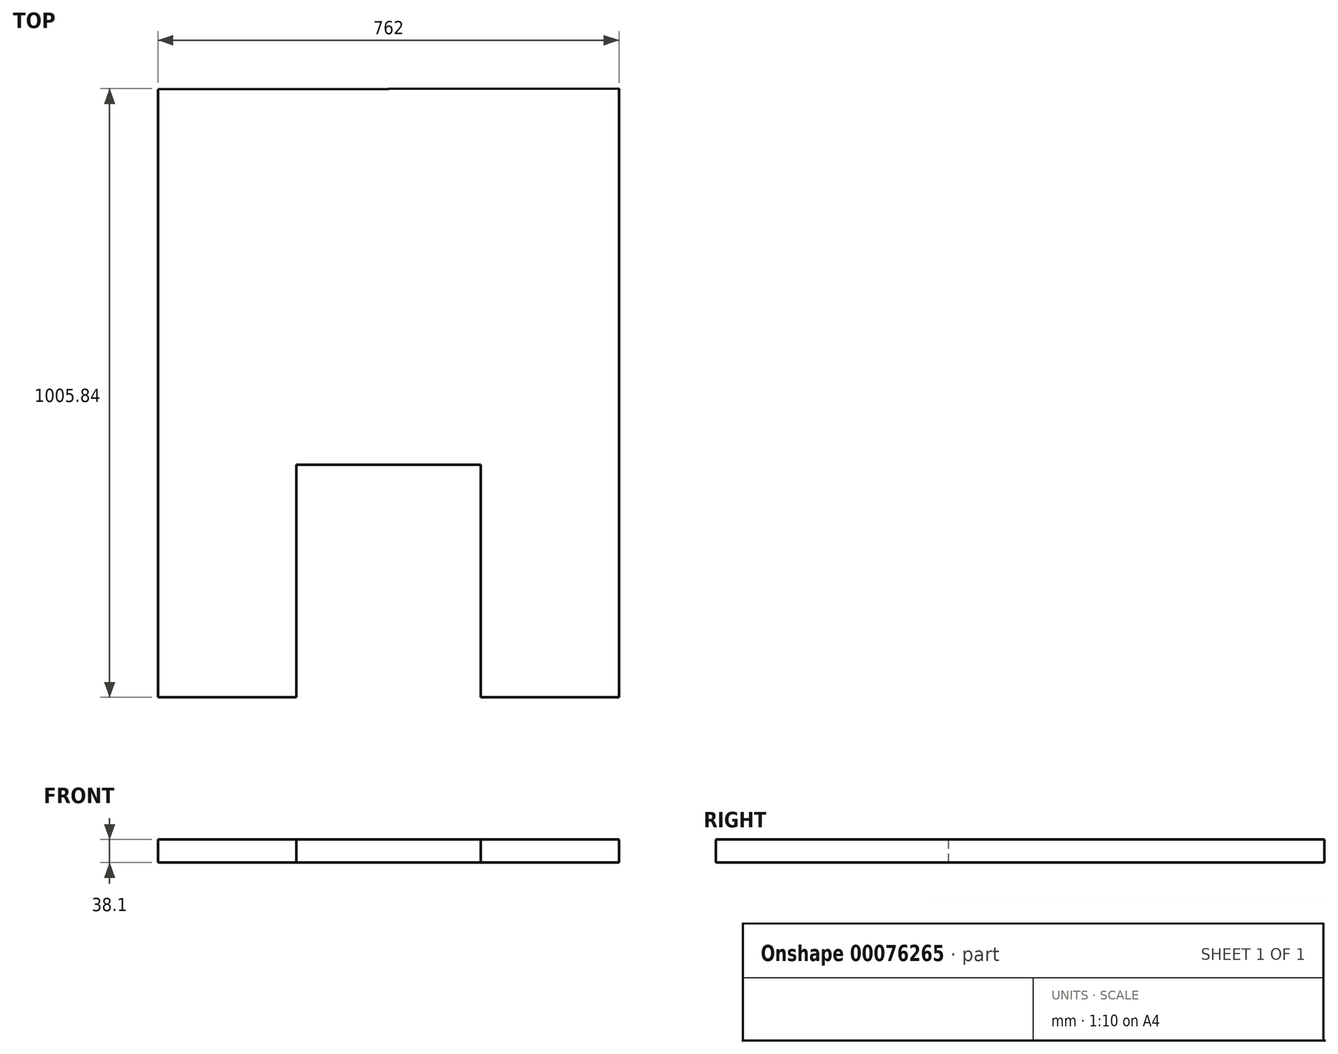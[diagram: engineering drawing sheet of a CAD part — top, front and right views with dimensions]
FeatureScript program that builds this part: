
annotation { "Feature Type Name" : "Feature", "Feature Type Description" : "" }
export const myFeature = defineFeature(function(context is Context, id is Id, definition is map)
    precondition{}
    {
        {
            var Q0;
            Q0=qCreatedBy(makeId("Top.planeOp"),FACE);
            var sketch = newSketch(context, id + "F0", { "sketchPlane" : qUnion([Q0])});
            skLineSegment(sketch, "E0", {"start": v(384.07, -567.13) * mm, "end": v(384.07, 438.71) * mm});
            skLineSegment(sketch, "E1", {"start": v(155.47, -182.5) * mm, "end": v(-149.33, -182.5) * mm});
            skLineSegment(sketch, "E2", {"start": v(-377.93, 437.62) * mm, "end": v(-377.93, -567.13) * mm});
            skLineSegment(sketch, "E3", {"start": v(-149.33, -182.5) * mm, "end": v(-149.33, -567.13) * mm});
            skLineSegment(sketch, "E4", {"start": v(155.47, -182.5) * mm, "end": v(155.47, -567.13) * mm});
            skLineSegment(sketch, "E5", {"start": v(-377.93, 437.62) * mm, "end": v(384.07, 438.71) * mm});
            skLineSegment(sketch, "E6", {"start": v(-377.93, -567.13) * mm, "end": v(-149.33, -567.13) * mm});
            skLineSegment(sketch, "E7", {"start": v(155.47, -567.13) * mm, "end": v(384.07, -567.13) * mm});
            skSolve(sketch);
        }
        {
            var Q0;
            Q0 = qSketchRegion(id + "F0", true);
            extrude(context, id + "F1", {"entities" : qUnion([Q0]), "depth" : 38.1 * mm});
        }
    });
